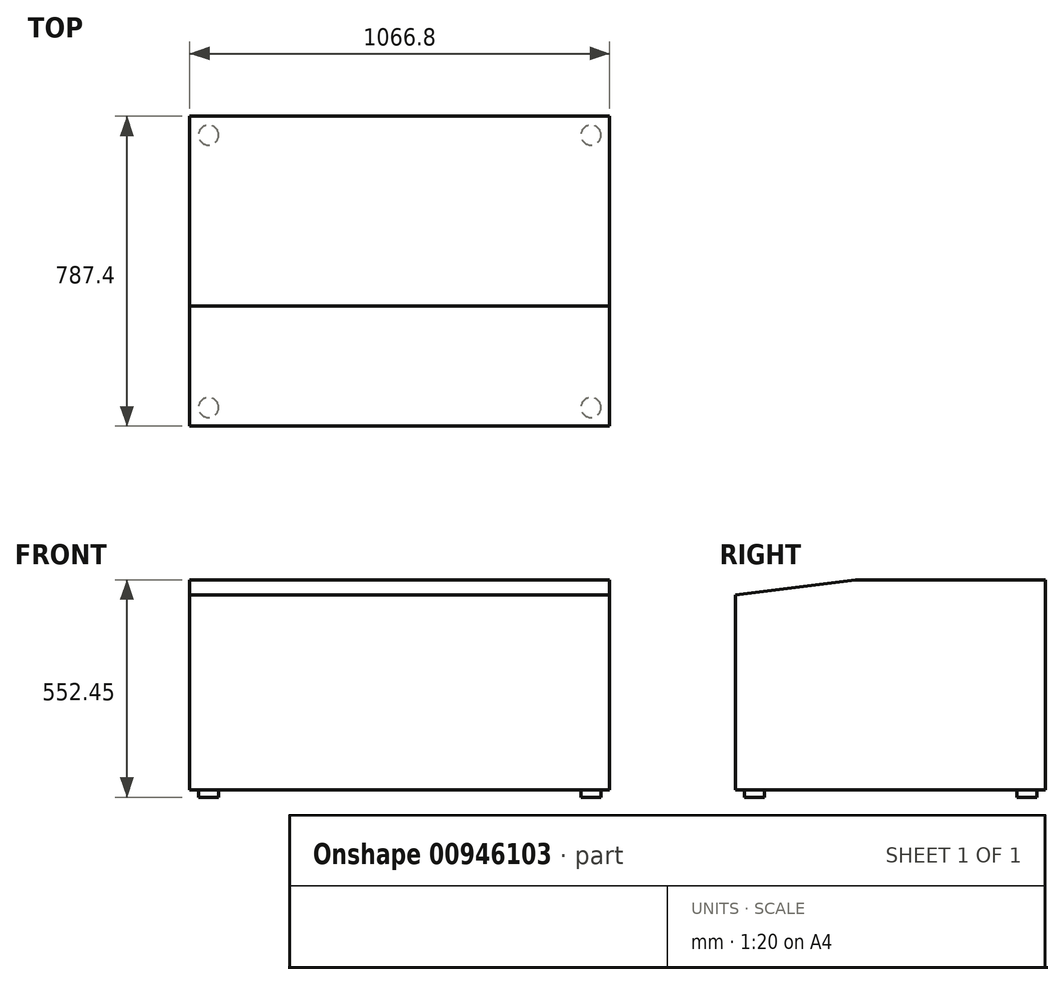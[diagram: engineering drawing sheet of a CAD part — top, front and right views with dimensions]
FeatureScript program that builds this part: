
annotation { "Feature Type Name" : "Feature", "Feature Type Description" : "" }
export const myFeature = defineFeature(function(context is Context, id is Id, definition is map)
    precondition{}
    {
        {
            var Q0;
            Q0=qCreatedBy(makeId("Top.planeOp"),FACE);
            var sketch = newSketch(context, id + "F0", { "sketchPlane" : qUnion([Q0])});
            skLineSegment(sketch, "E0.bottom", {"start": v(533.4, -393.7) * mm, "end": v(-533.4, -393.7) * mm});
            skLineSegment(sketch, "E0.top", {"start": v(533.4, 393.7) * mm, "end": v(-533.4, 393.7) * mm});
            skLineSegment(sketch, "E0.left", {"start": v(533.4, -393.7) * mm, "end": v(533.4, 393.7) * mm});
            skLineSegment(sketch, "E0.right", {"start": v(-533.4, -393.7) * mm, "end": v(-533.4, 393.7) * mm});
            skPoint(sketch, "E0.middle", {"position": v(0, 0) * mm});
            skSolve(sketch);
        }
        {
            var Q0;
            Q0 = qSketchRegion(id + "F0", true);
            extrude(context, id + "F1", {"entities" : qUnion([Q0]), "depth" : 533.4 * mm, "offsetDistance" : 25.4 * mm});
        }
        {
            var Q0;
            Q0=makeQuery(id+"F1.opExtrude","CAP_FACE",FACE,{"disambiguationData":[OSD([sQuery(id+"F0.wireOp",EDGE,"E0.bottom"),sQuery(id+"F0.wireOp",EDGE,"E0.top"),sQuery(id+"F0.wireOp",EDGE,"E0.left"),sQuery(id+"F0.wireOp",EDGE,"E0.right")])],"isStart":true});
            var sketch = newSketch(context, id + "F2", { "sketchPlane" : qUnion([Q0])});
            skCircle(sketch, "E1", {"center": v(-485.78, -346.07) * mm, "radius": 25.4 * mm});
            skSolve(sketch);
        }
        {
            var Q0;
            Q0 = qSketchRegion(id + "F2", true);
            extrude(context, id + "F3", {"entities" : qUnion([Q0]), "depth" : 19.05 * mm, "offsetDistance" : 25.4 * mm});
        }
        {
            var Q0;
            Q0=makeQuery(id+"F3.opExtrude","SWEPT_BODY",BODY,{"disambiguationData":[OSD([sQuery(id+"F2.wireOp",EDGE,"E1")])]});
            var Q1;
            Q1=qCreatedBy(makeId("Front.planeOp"),FACE);
            mirror(context, id + "F4", {"entities" : qUnion([Q0]), "mirrorPlane" : qUnion([Q1])});
        }
        {
            var Q0;
            Q0=makeQuery(id+"F3.opExtrude","SWEPT_BODY",BODY,{"disambiguationData":[OSD([sQuery(id+"F2.wireOp",EDGE,"E1")])]});
            var Q1;
            Q1=makeQuery(id+"F4.opPattern","COPY",BODY,{"derivedFrom":makeQuery(id+"F3.opExtrude","SWEPT_BODY",BODY,{"disambiguationData":[OSD([sQuery(id+"F2.wireOp",EDGE,"E1")])]}),"instanceName":"1"});
            var Q2;
            Q2=qCreatedBy(makeId("Right.planeOp"),FACE);
            mirror(context, id + "F5", {"entities" : qUnion([Q0, Q1]), "mirrorPlane" : qUnion([Q2])});
        }
        {
            var Q0;
            Q0=makeQuery(id+"F1.opExtrude","SWEPT_FACE",FACE,{"disambiguationData":[OSD([sQuery(id+"F0.wireOp",EDGE,"E0.right")])]});
            var sketch = newSketch(context, id + "F6", { "sketchPlane" : qUnion([Q0])});
            skLineSegment(sketch, "E2", {"start": v(88.9, 533.4) * mm, "end": v(393.7, 533.4) * mm});
            skLineSegment(sketch, "E3", {"start": v(393.7, 533.4) * mm, "end": v(393.7, 495.3) * mm});
            skLineSegment(sketch, "E4", {"start": v(393.7, 495.3) * mm, "end": v(88.9, 533.4) * mm});
            skSolve(sketch);
        }
        {
            var Q0;
            Q0 = qSketchRegion(id + "F6", true);
            extrude(context, id + "F7", {"entities" : qUnion([Q0]), "operationType" : NewBodyOperationType.REMOVE, "endBound" : BoundingType.THROUGH_ALL, "oppositeDirection" : true, "depth" : 25.4 * mm, "offsetDistance" : 25.4 * mm});
        }
    });
